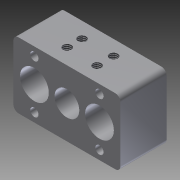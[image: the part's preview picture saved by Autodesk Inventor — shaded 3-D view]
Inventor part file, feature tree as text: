
AUTODESK INVENTOR PART (.ipt)
format: ipt  version: 2012 (Build 160160000, 160)  size: 144,896 bytes
history: native  units: in
note: dims shown in document units (in); Inventor stores cm internally (conversion verified against a paired STEP export)
features: thread x4, extrude x2, sketch x2, fillet x1
ambient origin geometry x8: Origin, YZ Plane, XZ Plane, XY Plane, X Axis, Y Axis, Z Axis, Center Point
bodies: Solid1 (feature_tree)
feature tree (9):
  extrude  "Extrusion1"  Depth=1.5748in
  fillet  "Fillet1"  Radius=0.689in
  extrude  "Extrusion2"  Depth=0.1969in
  thread  "Thread1"  [1 undecoded]
  thread  "Thread2"  [1 undecoded]
  thread  "Thread3"  [1 undecoded]
  thread  "Thread4"  [1 undecoded]
  sketch  "Sketch1"  dims[d0=2.5591in d1=1.5748in d4=0.689in]
  sketch  "Sketch2"  dims[d5=0.1969in d6=0.1969in d7=0.502in d8=0.502in d9=1.2795in d10=0.502in d11=0.5906in d12=1.1024in d13=0.0in d14=0.125in d15=0.1969in d16=0.1969in d19=0.7874in d21=0.7874in d22=0.1772in d23=0.1969in d24=0.5512in d25=1.1024in d26=0.5512in d27=0.0in d28=1.0in d29=0.0in d30=1.0in d31=0.0in d32=1.0in d33=0.0in d34=1.0in d35=0.0in]
note: 4 required parameter values undecoded (feature->parameter linkage not recoverable at this tier; creation-order binding heuristic only, values carry confidence <= 0.55)
